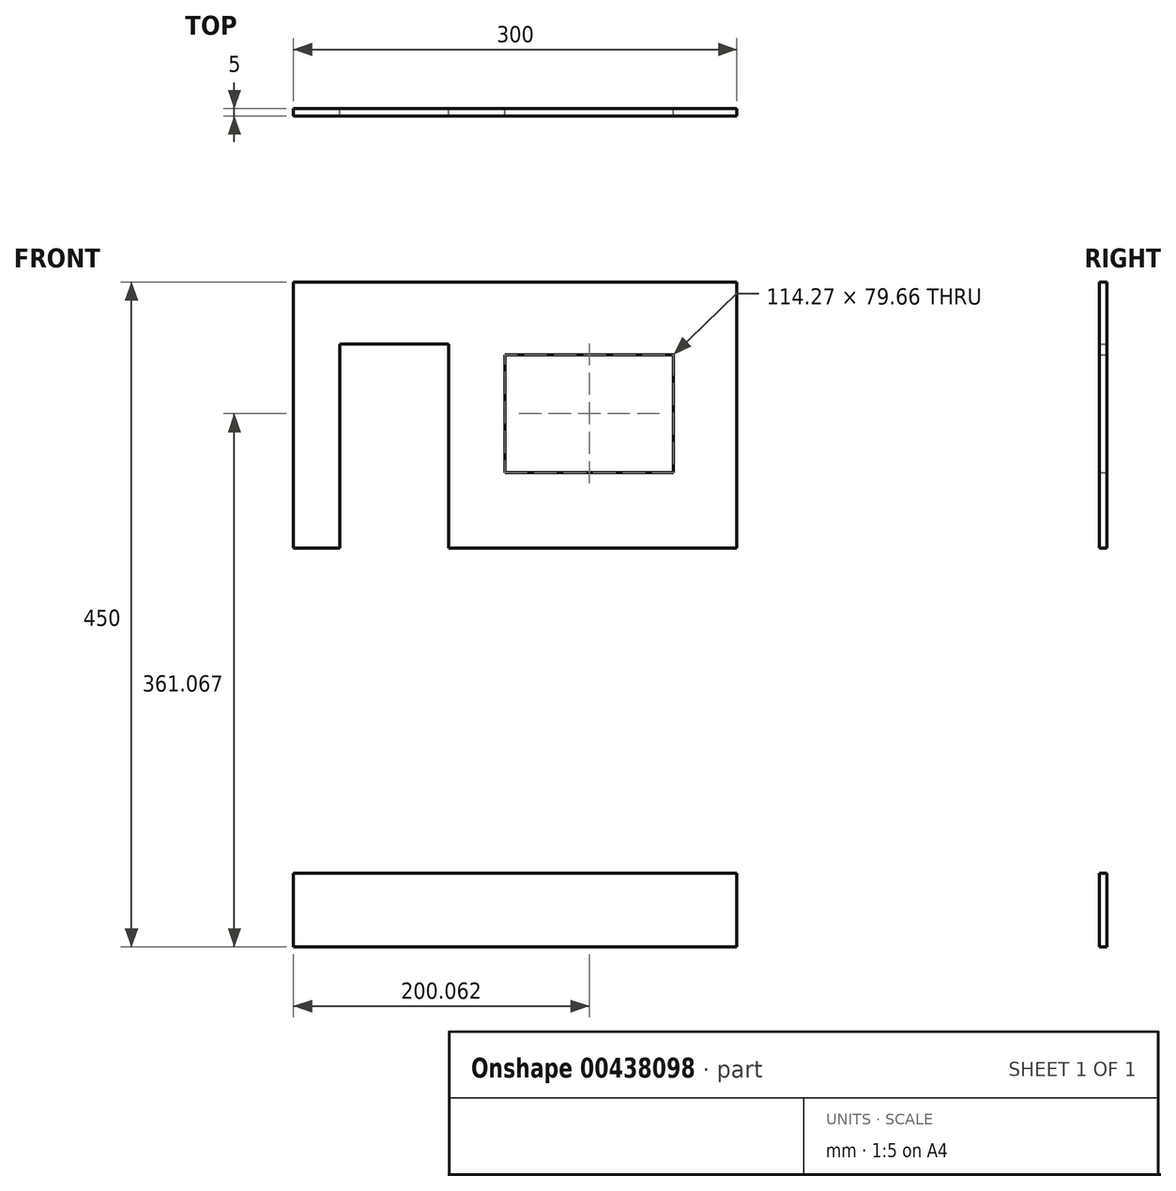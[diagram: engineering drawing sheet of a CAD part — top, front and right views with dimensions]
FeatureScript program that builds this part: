
annotation { "Feature Type Name" : "Feature", "Feature Type Description" : "" }
export const myFeature = defineFeature(function(context is Context, id is Id, definition is map)
    precondition{}
    {
        {
            var Q0;
            Q0=qCreatedBy(makeId("Front.planeOp"),FACE);
            var sketch = newSketch(context, id + "F0", { "sketchPlane" : qUnion([Q0])});
            skLineSegment(sketch, "E0.bottom", {"start": v(-277.25, 223.45) * mm, "end": v(22.75, 223.45) * mm});
            skLineSegment(sketch, "E0.top", {"start": v(-277.25, -226.55) * mm, "end": v(22.75, -226.55) * mm});
            skLineSegment(sketch, "E0.left", {"start": v(-277.25, 223.45) * mm, "end": v(-277.25, -226.55) * mm});
            skLineSegment(sketch, "E0.right", {"start": v(22.75, 223.45) * mm, "end": v(22.75, -226.55) * mm});
            skLineSegment(sketch, "E1", {"start": v(-277.25, -176.55) * mm, "end": v(22.75, -176.55) * mm});
            skLineSegment(sketch, "E2", {"start": v(-277.25, -176.55) * mm, "end": v(-277.25, -226.55) * mm});
            skLineSegment(sketch, "E3", {"start": v(22.75, -176.55) * mm, "end": v(22.75, -226.55) * mm});
            skPoint(sketch, "E4.startSnap0", {"position": v(-277.25, -1.55) * mm});
            skLineSegment(sketch, "E5", {"start": v(22.75, 0) * mm, "end": v(22.75, -176.55) * mm});
            skLineSegment(sketch, "E6", {"start": v(22.75, 23.2) * mm, "end": v(22.75, -16.8) * mm});
            skLineSegment(sketch, "E7", {"start": v(-277.25, -16.8) * mm, "end": v(-277.25, 23.2) * mm});
            skLineSegment(sketch, "E8", {"start": v(-127.25, 223.45) * mm, "end": v(-127.25, -176.55) * mm, "construction": true});
            skLineSegment(sketch, "E9", {"start": v(-195.02, -176.55) * mm, "end": v(-195.02, 3.45) * mm, "construction": true});
            skLineSegment(sketch, "E10", {"start": v(-191.28, 223.45) * mm, "end": v(-191.28, 43.45) * mm, "construction": true});
            skLineSegment(sketch, "E11", {"start": v(-277.25, 43.45) * mm, "end": v(22.75, 43.45) * mm});
            skLineSegment(sketch, "E12", {"start": v(22.75, 43.45) * mm, "end": v(22.75, 0) * mm});
            skLineSegment(sketch, "E13", {"start": v(-195.02, 3.45) * mm, "end": v(-277.25, 3.45) * mm});
            skLineSegment(sketch, "E14", {"start": v(-277.25, 3.45) * mm, "end": v(22.75, 3.45) * mm});
            skLineSegment(sketch, "E15.bottom", {"start": v(-245.98, 43.45) * mm, "end": v(-172.2, 43.45) * mm});
            skLineSegment(sketch, "E15.top", {"start": v(-245.98, 181.53) * mm, "end": v(-172.2, 181.53) * mm});
            skLineSegment(sketch, "E15.left", {"start": v(-245.98, 43.45) * mm, "end": v(-245.98, 181.53) * mm});
            skLineSegment(sketch, "E15.right", {"start": v(-172.2, 43.45) * mm, "end": v(-172.2, 181.53) * mm});
            skLineSegment(sketch, "E16.bottom", {"start": v(-20.05, 174.35) * mm, "end": v(-134.32, 174.35) * mm});
            skLineSegment(sketch, "E16.top", {"start": v(-20.05, 94.69) * mm, "end": v(-134.32, 94.69) * mm});
            skLineSegment(sketch, "E16.left", {"start": v(-20.05, 174.35) * mm, "end": v(-20.05, 94.69) * mm});
            skLineSegment(sketch, "E16.right", {"start": v(-134.32, 174.35) * mm, "end": v(-134.32, 94.69) * mm});
            skLineSegment(sketch, "E17.bottom", {"start": v(-11.56, -37.22) * mm, "end": v(-80.78, -37.22) * mm});
            skLineSegment(sketch, "E17.top", {"start": v(-11.56, -176.55) * mm, "end": v(-80.78, -176.55) * mm});
            skLineSegment(sketch, "E17.left", {"start": v(-11.56, -37.22) * mm, "end": v(-11.56, -176.55) * mm});
            skLineSegment(sketch, "E17.right", {"start": v(-80.78, -37.22) * mm, "end": v(-80.78, -176.55) * mm});
            skLineSegment(sketch, "E18.bottom", {"start": v(-230.97, -47.01) * mm, "end": v(-195.02, -47.01) * mm});
            skLineSegment(sketch, "E18.top", {"start": v(-230.97, -133.2) * mm, "end": v(-195.02, -133.2) * mm});
            skLineSegment(sketch, "E18.left", {"start": v(-230.97, -47.01) * mm, "end": v(-230.97, -133.2) * mm});
            skLineSegment(sketch, "E18.right", {"start": v(-195.02, -47.01) * mm, "end": v(-195.02, -133.2) * mm});
            skLineSegment(sketch, "E19.bottom", {"start": v(-176.77, -47.01) * mm, "end": v(-142.16, -47.01) * mm});
            skLineSegment(sketch, "E19.top", {"start": v(-176.77, -133.86) * mm, "end": v(-142.16, -133.86) * mm});
            skLineSegment(sketch, "E19.left", {"start": v(-176.77, -47.01) * mm, "end": v(-176.77, -133.86) * mm});
            skLineSegment(sketch, "E19.right", {"start": v(-142.16, -47.01) * mm, "end": v(-142.16, -133.86) * mm});
            skSolve(sketch);
        }
        {
            var Q0;
            {var subQ1=sQuery(id+"F0.wireOp",EDGE,"E0.bottom");Q0=makeQuery(id+"F0.imprint","IMPRINT",FACE,{"disambiguationData":[TD([[makeQuery(id+"F0.imprint","IMPRINT",EDGE,{"derivedFrom":subQ1}),-1.0]])]});}
            var Q1;
            {var subQ13=sQuery(id+"F0.wireOp",EDGE,"E5");Q1=makeQuery(id+"F0.imprint","IMPRINT",FACE,{"disambiguationData":[TD([[makeQuery(id+"F0.imprint","IMPRINT",EDGE,{"derivedFrom":subQ13}),-1.0]])]});}
            var Q2;
            {var subQ3=sQuery(id+"F0.wireOp",EDGE,"E15.bottom");Q2=makeQuery(id+"F0.imprint","IMPRINT",FACE,{"disambiguationData":[TD([[makeQuery(id+"F0.imprint","IMPRINT",EDGE,{"derivedFrom":subQ3}),-1.0]])]});}
            var Q3;
            Q3=makeQuery(id+"F0.imprint","IMPRINT",FACE,{"disambiguationData":[TD([[makeQuery(id+"F0.imprint","IMPRINT",EDGE,{"derivedFrom":sQuery(id+"F0.wireOp",EDGE,"E0.top")}),1.0]])]});
            extrude(context, id + "F1", {"entities" : qUnion([Q0, Q1, Q2, Q3]), "depth" : 5 * mm});
        }
    });
